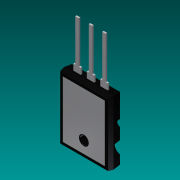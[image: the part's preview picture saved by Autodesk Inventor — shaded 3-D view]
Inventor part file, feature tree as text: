
AUTODESK INVENTOR PART (.ipt)
format: ipt  version: 2015 (Build 190159000, 159)  size: 577,536 bytes
history: native  units: mm
features: sketch x7, extrude x6, projected_geometry x4, fillet x2, hole x1, plane x1, emboss x1
ambient origin geometry x8: Origin, YZ Plane, XZ Plane, XY Plane, X Axis, Y Axis, Z Axis, Center Point
bodies: Solid1 (feature_tree)
feature tree (22):
  extrude  "Extrusion1"  Depth=26.0mm
  hole  "Hole1"  [1 undecoded]
  extrude  "Extrusion2"  Depth=4.35mm
  plane  "Work Plane1"
  extrude  "Extrusion3"  Depth=2.25mm
  extrude  "Extrusion4"  Depth=11.2mm
  fillet  "Fillet1"  Radius=3.0mm
  fillet  "Fillet2"  [1 undecoded]
  extrude  "Extrusion5"  Depth=5.0mm
  emboss  "Emboss1"
  extrude  "Extrusion6"  Depth=0.1mm
  sketch  "Sketch1"  dims[d0=20.0mm d1=26.0mm]
  sketch  "Sketch2"  dims[d2=3.0mm d3=2.0mm d4=-0.872665mm d5=-1.745329mm d6=6.3mm d7=1.0mm]
  sketch  "Sketch3"  dims[d8=3.5mm d9=6.0mm d10=4.0mm d11=2.0mm d12=90.0deg d13=8.0mm d14=20.594885mm d15=4.35mm]
  sketch  "Sketch4"  dims[d16=4.35mm d17=2.25mm]
  sketch  "Sketch5"  dims[d18=2.25mm d19=11.2mm d20=3.0mm d21=0.872665mm d22=-3.0mm]
  sketch  "Sketch6"  dims[d23=3.0mm d24=5.0mm]
  sketch  "Sketch7"  dims[d25=3.0mm d26=5.0mm d27=3.0mm d28=5.0mm d29=5.45mm d30=5.45mm d31=1.4mm d32=17.0mm d33=20.0mm d35=5.45mm d36=20.0mm d38=5.45mm d41=0.3mm d42=0.3mm d43=0.0mm d44=0.0mm d45=23.0mm d46=17.0mm d47=4.0mm d48=0.001mm d49=0.0mm d50=0.2mm d51=0.2mm d52=13.0mm d53=9.0mm d54=5.0mm d55=0.1mm d56=0.0mm d57=0.2mm d58=0.0mm d59=2.5mm d60=0.2mm d61=0.1mm d62=0.0mm]
  projected_geometry  "Project Cut Edges1"
  projected_geometry  "Project Cut Edges2"
  projected_geometry  "Project Cut Edges3"
  projected_geometry  "Project Cut Edges4"
note: 2 required parameter values undecoded (feature->parameter linkage not recoverable at this tier; creation-order binding heuristic only, values carry confidence <= 0.55)
